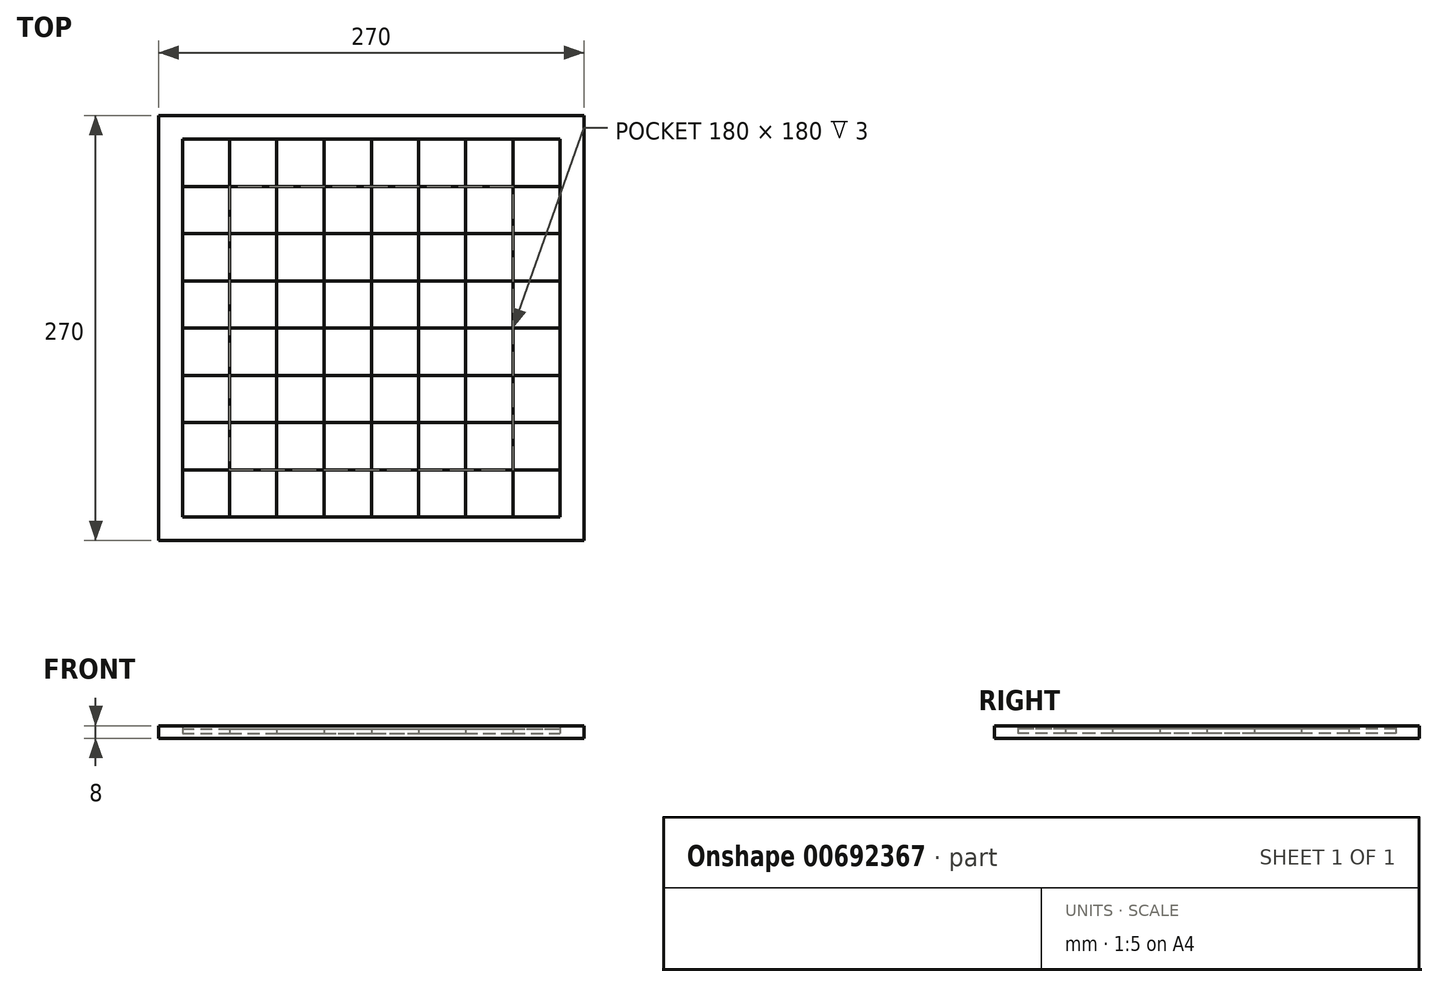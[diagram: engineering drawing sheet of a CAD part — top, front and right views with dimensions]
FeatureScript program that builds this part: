
annotation { "Feature Type Name" : "Feature", "Feature Type Description" : "" }
export const myFeature = defineFeature(function(context is Context, id is Id, definition is map)
    precondition{}
    {
        {
            var Q0;
            Q0=qCreatedBy(makeId("Top.planeOp"),FACE);
            var sketch = newSketch(context, id + "F0", { "sketchPlane" : qUnion([Q0])});
            skLineSegment(sketch, "E0.bottom", {"start": v(-120, 120) * mm, "end": v(120, 120) * mm});
            skLineSegment(sketch, "E0.top", {"start": v(-120, -120) * mm, "end": v(120, -120) * mm});
            skLineSegment(sketch, "E0.left", {"start": v(-120, 120) * mm, "end": v(-120, -120) * mm});
            skLineSegment(sketch, "E0.right", {"start": v(120, 120) * mm, "end": v(120, -120) * mm});
            skPoint(sketch, "E0.middle", {"position": v(0, 0) * mm});
            skLineSegment(sketch, "E1.0", {"start": v(-135, 135) * mm, "end": v(-135, -135) * mm});
            skLineSegment(sketch, "E1.1", {"start": v(-135, 135) * mm, "end": v(135, 135) * mm});
            skLineSegment(sketch, "E1.2", {"start": v(135, 135) * mm, "end": v(135, -135) * mm});
            skLineSegment(sketch, "E1.3", {"start": v(-135, -135) * mm, "end": v(135, -135) * mm});
            skLineSegment(sketch, "E2.0.1.0", {"start": v(-120, 90) * mm, "end": v(120, 90) * mm});
            skLineSegment(sketch, "E2.0.2.0", {"start": v(-120, 60) * mm, "end": v(120, 60) * mm});
            skLineSegment(sketch, "E2.0.3.0", {"start": v(-120, 30) * mm, "end": v(120, 30) * mm});
            skLineSegment(sketch, "E2.0.4.0", {"start": v(-120, 0) * mm, "end": v(120, 0) * mm});
            skLineSegment(sketch, "E2.0.5.0", {"start": v(-120, -30) * mm, "end": v(120, -30) * mm});
            skLineSegment(sketch, "E2.0.6.0", {"start": v(-120, -60) * mm, "end": v(120, -60) * mm});
            skLineSegment(sketch, "E2.0.7.0", {"start": v(-120, -90) * mm, "end": v(120, -90) * mm});
            skLineSegment(sketch, "E2.direction2", {"start": v(-120, 120) * mm, "end": v(-120, 90) * mm, "construction": true});
            skLineSegment(sketch, "E3.1.0.0", {"start": v(-90, 120) * mm, "end": v(-90, -120) * mm});
            skLineSegment(sketch, "E3.2.0.0", {"start": v(-60, 120) * mm, "end": v(-60, -120) * mm});
            skLineSegment(sketch, "E3.3.0.0", {"start": v(-30, 120) * mm, "end": v(-30, -120) * mm});
            skLineSegment(sketch, "E3.4.0.0", {"start": v(0, 120) * mm, "end": v(0, -120) * mm});
            skLineSegment(sketch, "E3.5.0.0", {"start": v(30, 120) * mm, "end": v(30, -120) * mm});
            skLineSegment(sketch, "E3.6.0.0", {"start": v(60, 120) * mm, "end": v(60, -120) * mm});
            skLineSegment(sketch, "E3.7.0.0", {"start": v(90, 120) * mm, "end": v(90, -120) * mm});
            skSolve(sketch);
        }
        {
            var Q0;
            {var subQ0=sQuery(id+"F0.wireOp",EDGE,"E3.2.0.0");var subQ1=sQuery(id+"F0.wireOp",EDGE,"E2.0.2.0");var subQ2=makeQuery(id+"F0.imprint","INTERSECT",VERTEX,{"derivedFrom":[subQ1,subQ0]});Q0=makeQuery(id+"F0.imprint","IMPRINT",FACE,{"disambiguationData":[TD([[makeQuery(id+"F0.imprint","IMPRINT",EDGE,{"disambiguationData":[TD([[subQ2,-1.0]])],"derivedFrom":subQ1}),-1.0]])]});}
            var Q1;
            {var subQ0=sQuery(id+"F0.wireOp",EDGE,"E0.right");var subQ1=sQuery(id+"F0.wireOp",EDGE,"E0.bottom");var subQ2=makeQuery(id+"F0.imprint","INTERSECT",VERTEX,{"derivedFrom":[subQ1,subQ0]});Q1=makeQuery(id+"F0.imprint","IMPRINT",FACE,{"disambiguationData":[TD([[makeQuery(id+"F0.imprint","IMPRINT",EDGE,{"disambiguationData":[TD([[subQ2,1.0]])],"derivedFrom":subQ1}),-1.0]])]});}
            var Q2;
            {var subQ0=sQuery(id+"F0.wireOp",EDGE,"E2.0.2.0");var subQ1=sQuery(id+"F0.wireOp",EDGE,"E0.right");var subQ2=makeQuery(id+"F0.imprint","INTERSECT",VERTEX,{"derivedFrom":[subQ1,subQ0]});Q2=makeQuery(id+"F0.imprint","IMPRINT",FACE,{"disambiguationData":[TD([[makeQuery(id+"F0.imprint","IMPRINT",EDGE,{"disambiguationData":[TD([[subQ2,-1.0]])],"derivedFrom":subQ1}),-1.0]])]});}
            var Q3;
            {var subQ0=sQuery(id+"F0.wireOp",EDGE,"E3.6.0.0");var subQ1=sQuery(id+"F0.wireOp",EDGE,"E2.0.4.0");var subQ2=makeQuery(id+"F0.imprint","INTERSECT",VERTEX,{"derivedFrom":[subQ1,subQ0]});Q3=makeQuery(id+"F0.imprint","IMPRINT",FACE,{"disambiguationData":[TD([[makeQuery(id+"F0.imprint","IMPRINT",EDGE,{"disambiguationData":[TD([[subQ2,-1.0]])],"derivedFrom":subQ1}),-1.0]])]});}
            var Q4;
            {var subQ0=sQuery(id+"F0.wireOp",EDGE,"E3.4.0.0");var subQ1=sQuery(id+"F0.wireOp",EDGE,"E0.top");var subQ2=makeQuery(id+"F0.imprint","INTERSECT",VERTEX,{"derivedFrom":[subQ1,subQ0]});Q4=makeQuery(id+"F0.imprint","IMPRINT",FACE,{"disambiguationData":[TD([[makeQuery(id+"F0.imprint","IMPRINT",EDGE,{"disambiguationData":[TD([[subQ2,-1.0]])],"derivedFrom":subQ1}),1.0]])]});}
            var Q5;
            {var subQ0=sQuery(id+"F0.wireOp",EDGE,"E3.5.0.0");var subQ1=sQuery(id+"F0.wireOp",EDGE,"E2.0.2.0");var subQ2=makeQuery(id+"F0.imprint","INTERSECT",VERTEX,{"derivedFrom":[subQ1,subQ0]});Q5=makeQuery(id+"F0.imprint","IMPRINT",FACE,{"disambiguationData":[TD([[makeQuery(id+"F0.imprint","IMPRINT",EDGE,{"disambiguationData":[TD([[subQ2,-1.0]])],"derivedFrom":subQ1}),-1.0]])]});}
            var Q6;
            {var subQ0=sQuery(id+"F0.wireOp",EDGE,"E2.0.1.0");var subQ1=sQuery(id+"F0.wireOp",EDGE,"E0.right");var subQ2=makeQuery(id+"F0.imprint","INTERSECT",VERTEX,{"derivedFrom":[subQ1,subQ0]});Q6=makeQuery(id+"F0.imprint","IMPRINT",FACE,{"disambiguationData":[TD([[makeQuery(id+"F0.imprint","IMPRINT",EDGE,{"disambiguationData":[TD([[subQ2,-1.0]])],"derivedFrom":subQ1}),-1.0]])]});}
            var Q7;
            {var subQ0=sQuery(id+"F0.wireOp",EDGE,"E3.3.0.0");var subQ1=sQuery(id+"F0.wireOp",EDGE,"E2.0.5.0");var subQ2=makeQuery(id+"F0.imprint","INTERSECT",VERTEX,{"derivedFrom":[subQ1,subQ0]});Q7=makeQuery(id+"F0.imprint","IMPRINT",FACE,{"disambiguationData":[TD([[makeQuery(id+"F0.imprint","IMPRINT",EDGE,{"disambiguationData":[TD([[subQ2,-1.0]])],"derivedFrom":subQ1}),-1.0]])]});}
            var Q8;
            {var subQ0=sQuery(id+"F0.wireOp",EDGE,"E0.right");var subQ1=sQuery(id+"F0.wireOp",EDGE,"E0.top");var subQ2=makeQuery(id+"F0.imprint","INTERSECT",VERTEX,{"derivedFrom":[subQ1,subQ0]});Q8=makeQuery(id+"F0.imprint","IMPRINT",FACE,{"disambiguationData":[TD([[makeQuery(id+"F0.imprint","IMPRINT",EDGE,{"disambiguationData":[TD([[subQ2,1.0]])],"derivedFrom":subQ1}),1.0]])]});}
            var Q9;
            {var subQ0=sQuery(id+"F0.wireOp",EDGE,"E0.left");var subQ1=sQuery(id+"F0.wireOp",EDGE,"E0.bottom");var subQ2=makeQuery(id+"F0.imprint","INTERSECT",VERTEX,{"derivedFrom":[subQ1,subQ0]});Q9=makeQuery(id+"F0.imprint","IMPRINT",FACE,{"disambiguationData":[TD([[makeQuery(id+"F0.imprint","IMPRINT",EDGE,{"disambiguationData":[TD([[subQ2,-1.0]])],"derivedFrom":subQ1}),-1.0]])]});}
            var Q10;
            {var subQ0=sQuery(id+"F0.wireOp",EDGE,"E3.3.0.0");var subQ1=sQuery(id+"F0.wireOp",EDGE,"E0.top");var subQ2=makeQuery(id+"F0.imprint","INTERSECT",VERTEX,{"derivedFrom":[subQ1,subQ0]});Q10=makeQuery(id+"F0.imprint","IMPRINT",FACE,{"disambiguationData":[TD([[makeQuery(id+"F0.imprint","IMPRINT",EDGE,{"disambiguationData":[TD([[subQ2,-1.0]])],"derivedFrom":subQ1}),1.0]])]});}
            var Q11;
            {var subQ0=sQuery(id+"F0.wireOp",EDGE,"E2.0.1.0");var subQ1=sQuery(id+"F0.wireOp",EDGE,"E0.left");var subQ2=makeQuery(id+"F0.imprint","INTERSECT",VERTEX,{"derivedFrom":[subQ1,subQ0]});Q11=makeQuery(id+"F0.imprint","IMPRINT",FACE,{"disambiguationData":[TD([[makeQuery(id+"F0.imprint","IMPRINT",EDGE,{"disambiguationData":[TD([[subQ2,-1.0]])],"derivedFrom":subQ1}),1.0]])]});}
            var Q12;
            {var subQ0=sQuery(id+"F0.wireOp",EDGE,"E2.0.5.0");var subQ1=sQuery(id+"F0.wireOp",EDGE,"E0.left");var subQ2=makeQuery(id+"F0.imprint","INTERSECT",VERTEX,{"derivedFrom":[subQ1,subQ0]});Q12=makeQuery(id+"F0.imprint","IMPRINT",FACE,{"disambiguationData":[TD([[makeQuery(id+"F0.imprint","IMPRINT",EDGE,{"disambiguationData":[TD([[subQ2,-1.0]])],"derivedFrom":subQ1}),1.0]])]});}
            var Q13;
            {var subQ0=sQuery(id+"F0.wireOp",EDGE,"E2.0.4.0");var subQ1=sQuery(id+"F0.wireOp",EDGE,"E0.left");var subQ2=makeQuery(id+"F0.imprint","INTERSECT",VERTEX,{"derivedFrom":[subQ1,subQ0]});Q13=makeQuery(id+"F0.imprint","IMPRINT",FACE,{"disambiguationData":[TD([[makeQuery(id+"F0.imprint","IMPRINT",EDGE,{"disambiguationData":[TD([[subQ2,-1.0]])],"derivedFrom":subQ1}),1.0]])]});}
            var Q14;
            {var subQ0=sQuery(id+"F0.wireOp",EDGE,"E3.5.0.0");var subQ1=sQuery(id+"F0.wireOp",EDGE,"E2.0.1.0");var subQ2=makeQuery(id+"F0.imprint","INTERSECT",VERTEX,{"derivedFrom":[subQ1,subQ0]});Q14=makeQuery(id+"F0.imprint","IMPRINT",FACE,{"disambiguationData":[TD([[makeQuery(id+"F0.imprint","IMPRINT",EDGE,{"disambiguationData":[TD([[subQ2,-1.0]])],"derivedFrom":subQ1}),-1.0]])]});}
            var Q15;
            {var subQ0=sQuery(id+"F0.wireOp",EDGE,"E2.0.5.0");var subQ1=sQuery(id+"F0.wireOp",EDGE,"E0.right");var subQ2=makeQuery(id+"F0.imprint","INTERSECT",VERTEX,{"derivedFrom":[subQ1,subQ0]});Q15=makeQuery(id+"F0.imprint","IMPRINT",FACE,{"disambiguationData":[TD([[makeQuery(id+"F0.imprint","IMPRINT",EDGE,{"disambiguationData":[TD([[subQ2,-1.0]])],"derivedFrom":subQ1}),-1.0]])]});}
            var Q16;
            {var subQ0=sQuery(id+"F0.wireOp",EDGE,"E3.3.0.0");var subQ1=sQuery(id+"F0.wireOp",EDGE,"E2.0.3.0");var subQ2=makeQuery(id+"F0.imprint","INTERSECT",VERTEX,{"derivedFrom":[subQ1,subQ0]});Q16=makeQuery(id+"F0.imprint","IMPRINT",FACE,{"disambiguationData":[TD([[makeQuery(id+"F0.imprint","IMPRINT",EDGE,{"disambiguationData":[TD([[subQ2,-1.0]])],"derivedFrom":subQ1}),-1.0]])]});}
            var Q17;
            {var subQ0=sQuery(id+"F0.wireOp",EDGE,"E0.left");var subQ1=sQuery(id+"F0.wireOp",EDGE,"E0.top");var subQ2=makeQuery(id+"F0.imprint","INTERSECT",VERTEX,{"derivedFrom":[subQ1,subQ0]});Q17=makeQuery(id+"F0.imprint","IMPRINT",FACE,{"disambiguationData":[TD([[makeQuery(id+"F0.imprint","IMPRINT",EDGE,{"disambiguationData":[TD([[subQ2,-1.0]])],"derivedFrom":subQ1}),1.0]])]});}
            var Q18;
            {var subQ0=sQuery(id+"F0.wireOp",EDGE,"E3.6.0.0");var subQ1=sQuery(id+"F0.wireOp",EDGE,"E0.bottom");var subQ2=makeQuery(id+"F0.imprint","INTERSECT",VERTEX,{"derivedFrom":[subQ1,subQ0]});Q18=makeQuery(id+"F0.imprint","IMPRINT",FACE,{"disambiguationData":[TD([[makeQuery(id+"F0.imprint","IMPRINT",EDGE,{"disambiguationData":[TD([[subQ2,-1.0]])],"derivedFrom":subQ1}),-1.0]])]});}
            var Q19;
            {var subQ0=sQuery(id+"F0.wireOp",EDGE,"E3.6.0.0");var subQ1=sQuery(id+"F0.wireOp",EDGE,"E2.0.2.0");var subQ2=makeQuery(id+"F0.imprint","INTERSECT",VERTEX,{"derivedFrom":[subQ1,subQ0]});Q19=makeQuery(id+"F0.imprint","IMPRINT",FACE,{"disambiguationData":[TD([[makeQuery(id+"F0.imprint","IMPRINT",EDGE,{"disambiguationData":[TD([[subQ2,-1.0]])],"derivedFrom":subQ1}),-1.0]])]});}
            var Q20;
            {var subQ0=sQuery(id+"F0.wireOp",EDGE,"E3.1.0.0");var subQ1=sQuery(id+"F0.wireOp",EDGE,"E2.0.6.0");var subQ2=makeQuery(id+"F0.imprint","INTERSECT",VERTEX,{"derivedFrom":[subQ1,subQ0]});Q20=makeQuery(id+"F0.imprint","IMPRINT",FACE,{"disambiguationData":[TD([[makeQuery(id+"F0.imprint","IMPRINT",EDGE,{"disambiguationData":[TD([[subQ2,-1.0]])],"derivedFrom":subQ1}),-1.0]])]});}
            var Q21;
            {var subQ0=sQuery(id+"F0.wireOp",EDGE,"E3.4.0.0");var subQ1=sQuery(id+"F0.wireOp",EDGE,"E2.0.3.0");var subQ2=makeQuery(id+"F0.imprint","INTERSECT",VERTEX,{"derivedFrom":[subQ1,subQ0]});Q21=makeQuery(id+"F0.imprint","IMPRINT",FACE,{"disambiguationData":[TD([[makeQuery(id+"F0.imprint","IMPRINT",EDGE,{"disambiguationData":[TD([[subQ2,-1.0]])],"derivedFrom":subQ1}),-1.0]])]});}
            var Q22;
            {var subQ0=sQuery(id+"F0.wireOp",EDGE,"E2.0.6.0");var subQ1=sQuery(id+"F0.wireOp",EDGE,"E0.left");var subQ2=makeQuery(id+"F0.imprint","INTERSECT",VERTEX,{"derivedFrom":[subQ1,subQ0]});Q22=makeQuery(id+"F0.imprint","IMPRINT",FACE,{"disambiguationData":[TD([[makeQuery(id+"F0.imprint","IMPRINT",EDGE,{"disambiguationData":[TD([[subQ2,-1.0]])],"derivedFrom":subQ1}),1.0]])]});}
            var Q23;
            {var subQ0=sQuery(id+"F0.wireOp",EDGE,"E3.1.0.0");var subQ1=sQuery(id+"F0.wireOp",EDGE,"E0.top");var subQ2=makeQuery(id+"F0.imprint","INTERSECT",VERTEX,{"derivedFrom":[subQ1,subQ0]});Q23=makeQuery(id+"F0.imprint","IMPRINT",FACE,{"disambiguationData":[TD([[makeQuery(id+"F0.imprint","IMPRINT",EDGE,{"disambiguationData":[TD([[subQ2,-1.0]])],"derivedFrom":subQ1}),1.0]])]});}
            var Q24;
            {var subQ0=sQuery(id+"F0.wireOp",EDGE,"E2.0.6.0");var subQ1=sQuery(id+"F0.wireOp",EDGE,"E0.right");var subQ2=makeQuery(id+"F0.imprint","INTERSECT",VERTEX,{"derivedFrom":[subQ1,subQ0]});Q24=makeQuery(id+"F0.imprint","IMPRINT",FACE,{"disambiguationData":[TD([[makeQuery(id+"F0.imprint","IMPRINT",EDGE,{"disambiguationData":[TD([[subQ2,-1.0]])],"derivedFrom":subQ1}),-1.0]])]});}
            var Q25;
            {var subQ0=sQuery(id+"F0.wireOp",EDGE,"E3.3.0.0");var subQ1=sQuery(id+"F0.wireOp",EDGE,"E2.0.4.0");var subQ2=makeQuery(id+"F0.imprint","INTERSECT",VERTEX,{"derivedFrom":[subQ1,subQ0]});Q25=makeQuery(id+"F0.imprint","IMPRINT",FACE,{"disambiguationData":[TD([[makeQuery(id+"F0.imprint","IMPRINT",EDGE,{"disambiguationData":[TD([[subQ2,-1.0]])],"derivedFrom":subQ1}),-1.0]])]});}
            var Q26;
            {var subQ0=sQuery(id+"F0.wireOp",EDGE,"E3.5.0.0");var subQ1=sQuery(id+"F0.wireOp",EDGE,"E0.top");var subQ2=makeQuery(id+"F0.imprint","INTERSECT",VERTEX,{"derivedFrom":[subQ1,subQ0]});Q26=makeQuery(id+"F0.imprint","IMPRINT",FACE,{"disambiguationData":[TD([[makeQuery(id+"F0.imprint","IMPRINT",EDGE,{"disambiguationData":[TD([[subQ2,-1.0]])],"derivedFrom":subQ1}),1.0]])]});}
            var Q27;
            {var subQ0=sQuery(id+"F0.wireOp",EDGE,"E3.2.0.0");var subQ1=sQuery(id+"F0.wireOp",EDGE,"E0.top");var subQ2=makeQuery(id+"F0.imprint","INTERSECT",VERTEX,{"derivedFrom":[subQ1,subQ0]});Q27=makeQuery(id+"F0.imprint","IMPRINT",FACE,{"disambiguationData":[TD([[makeQuery(id+"F0.imprint","IMPRINT",EDGE,{"disambiguationData":[TD([[subQ2,-1.0]])],"derivedFrom":subQ1}),1.0]])]});}
            var Q28;
            {var subQ0=sQuery(id+"F0.wireOp",EDGE,"E3.4.0.0");var subQ1=sQuery(id+"F0.wireOp",EDGE,"E2.0.6.0");var subQ2=makeQuery(id+"F0.imprint","INTERSECT",VERTEX,{"derivedFrom":[subQ1,subQ0]});Q28=makeQuery(id+"F0.imprint","IMPRINT",FACE,{"disambiguationData":[TD([[makeQuery(id+"F0.imprint","IMPRINT",EDGE,{"disambiguationData":[TD([[subQ2,-1.0]])],"derivedFrom":subQ1}),-1.0]])]});}
            var Q29;
            {var subQ0=sQuery(id+"F0.wireOp",EDGE,"E3.1.0.0");var subQ1=sQuery(id+"F0.wireOp",EDGE,"E2.0.5.0");var subQ2=makeQuery(id+"F0.imprint","INTERSECT",VERTEX,{"derivedFrom":[subQ1,subQ0]});Q29=makeQuery(id+"F0.imprint","IMPRINT",FACE,{"disambiguationData":[TD([[makeQuery(id+"F0.imprint","IMPRINT",EDGE,{"disambiguationData":[TD([[subQ2,-1.0]])],"derivedFrom":subQ1}),-1.0]])]});}
            var Q30;
            {var subQ0=sQuery(id+"F0.wireOp",EDGE,"E3.6.0.0");var subQ1=sQuery(id+"F0.wireOp",EDGE,"E2.0.3.0");var subQ2=makeQuery(id+"F0.imprint","INTERSECT",VERTEX,{"derivedFrom":[subQ1,subQ0]});Q30=makeQuery(id+"F0.imprint","IMPRINT",FACE,{"disambiguationData":[TD([[makeQuery(id+"F0.imprint","IMPRINT",EDGE,{"disambiguationData":[TD([[subQ2,-1.0]])],"derivedFrom":subQ1}),-1.0]])]});}
            var Q31;
            {var subQ0=sQuery(id+"F0.wireOp",EDGE,"E3.2.0.0");var subQ1=sQuery(id+"F0.wireOp",EDGE,"E2.0.1.0");var subQ2=makeQuery(id+"F0.imprint","INTERSECT",VERTEX,{"derivedFrom":[subQ1,subQ0]});Q31=makeQuery(id+"F0.imprint","IMPRINT",FACE,{"disambiguationData":[TD([[makeQuery(id+"F0.imprint","IMPRINT",EDGE,{"disambiguationData":[TD([[subQ2,-1.0]])],"derivedFrom":subQ1}),-1.0]])]});}
            var Q32;
            {var subQ0=sQuery(id+"F0.wireOp",EDGE,"E3.3.0.0");var subQ1=sQuery(id+"F0.wireOp",EDGE,"E2.0.2.0");var subQ2=makeQuery(id+"F0.imprint","INTERSECT",VERTEX,{"derivedFrom":[subQ1,subQ0]});Q32=makeQuery(id+"F0.imprint","IMPRINT",FACE,{"disambiguationData":[TD([[makeQuery(id+"F0.imprint","IMPRINT",EDGE,{"disambiguationData":[TD([[subQ2,-1.0]])],"derivedFrom":subQ1}),-1.0]])]});}
            var Q33;
            {var subQ0=sQuery(id+"F0.wireOp",EDGE,"E3.4.0.0");var subQ1=sQuery(id+"F0.wireOp",EDGE,"E2.0.5.0");var subQ2=makeQuery(id+"F0.imprint","INTERSECT",VERTEX,{"derivedFrom":[subQ1,subQ0]});Q33=makeQuery(id+"F0.imprint","IMPRINT",FACE,{"disambiguationData":[TD([[makeQuery(id+"F0.imprint","IMPRINT",EDGE,{"disambiguationData":[TD([[subQ2,-1.0]])],"derivedFrom":subQ1}),-1.0]])]});}
            var Q34;
            {var subQ0=sQuery(id+"F0.wireOp",EDGE,"E3.4.0.0");var subQ1=sQuery(id+"F0.wireOp",EDGE,"E0.bottom");var subQ2=makeQuery(id+"F0.imprint","INTERSECT",VERTEX,{"derivedFrom":[subQ1,subQ0]});Q34=makeQuery(id+"F0.imprint","IMPRINT",FACE,{"disambiguationData":[TD([[makeQuery(id+"F0.imprint","IMPRINT",EDGE,{"disambiguationData":[TD([[subQ2,-1.0]])],"derivedFrom":subQ1}),-1.0]])]});}
            var Q35;
            {var subQ0=sQuery(id+"F0.wireOp",EDGE,"E3.5.0.0");var subQ1=sQuery(id+"F0.wireOp",EDGE,"E0.bottom");var subQ2=makeQuery(id+"F0.imprint","INTERSECT",VERTEX,{"derivedFrom":[subQ1,subQ0]});Q35=makeQuery(id+"F0.imprint","IMPRINT",FACE,{"disambiguationData":[TD([[makeQuery(id+"F0.imprint","IMPRINT",EDGE,{"disambiguationData":[TD([[subQ2,-1.0]])],"derivedFrom":subQ1}),-1.0]])]});}
            var Q36;
            {var subQ0=sQuery(id+"F0.wireOp",EDGE,"E3.3.0.0");var subQ1=sQuery(id+"F0.wireOp",EDGE,"E0.bottom");var subQ2=makeQuery(id+"F0.imprint","INTERSECT",VERTEX,{"derivedFrom":[subQ1,subQ0]});Q36=makeQuery(id+"F0.imprint","IMPRINT",FACE,{"disambiguationData":[TD([[makeQuery(id+"F0.imprint","IMPRINT",EDGE,{"disambiguationData":[TD([[subQ2,-1.0]])],"derivedFrom":subQ1}),-1.0]])]});}
            var Q37;
            {var subQ0=sQuery(id+"F0.wireOp",EDGE,"E3.2.0.0");var subQ1=sQuery(id+"F0.wireOp",EDGE,"E0.bottom");var subQ2=makeQuery(id+"F0.imprint","INTERSECT",VERTEX,{"derivedFrom":[subQ1,subQ0]});Q37=makeQuery(id+"F0.imprint","IMPRINT",FACE,{"disambiguationData":[TD([[makeQuery(id+"F0.imprint","IMPRINT",EDGE,{"disambiguationData":[TD([[subQ2,-1.0]])],"derivedFrom":subQ1}),-1.0]])]});}
            var Q38;
            {var subQ0=sQuery(id+"F0.wireOp",EDGE,"E3.6.0.0");var subQ1=sQuery(id+"F0.wireOp",EDGE,"E0.top");var subQ2=makeQuery(id+"F0.imprint","INTERSECT",VERTEX,{"derivedFrom":[subQ1,subQ0]});Q38=makeQuery(id+"F0.imprint","IMPRINT",FACE,{"disambiguationData":[TD([[makeQuery(id+"F0.imprint","IMPRINT",EDGE,{"disambiguationData":[TD([[subQ2,-1.0]])],"derivedFrom":subQ1}),1.0]])]});}
            var Q39;
            {var subQ0=sQuery(id+"F0.wireOp",EDGE,"E3.2.0.0");var subQ1=sQuery(id+"F0.wireOp",EDGE,"E2.0.6.0");var subQ2=makeQuery(id+"F0.imprint","INTERSECT",VERTEX,{"derivedFrom":[subQ1,subQ0]});Q39=makeQuery(id+"F0.imprint","IMPRINT",FACE,{"disambiguationData":[TD([[makeQuery(id+"F0.imprint","IMPRINT",EDGE,{"disambiguationData":[TD([[subQ2,-1.0]])],"derivedFrom":subQ1}),-1.0]])]});}
            var Q40;
            {var subQ0=sQuery(id+"F0.wireOp",EDGE,"E3.1.0.0");var subQ1=sQuery(id+"F0.wireOp",EDGE,"E0.bottom");var subQ2=makeQuery(id+"F0.imprint","INTERSECT",VERTEX,{"derivedFrom":[subQ1,subQ0]});Q40=makeQuery(id+"F0.imprint","IMPRINT",FACE,{"disambiguationData":[TD([[makeQuery(id+"F0.imprint","IMPRINT",EDGE,{"disambiguationData":[TD([[subQ2,-1.0]])],"derivedFrom":subQ1}),-1.0]])]});}
            var Q41;
            {var subQ0=sQuery(id+"F0.wireOp",EDGE,"E3.5.0.0");var subQ1=sQuery(id+"F0.wireOp",EDGE,"E2.0.6.0");var subQ2=makeQuery(id+"F0.imprint","INTERSECT",VERTEX,{"derivedFrom":[subQ1,subQ0]});Q41=makeQuery(id+"F0.imprint","IMPRINT",FACE,{"disambiguationData":[TD([[makeQuery(id+"F0.imprint","IMPRINT",EDGE,{"disambiguationData":[TD([[subQ2,-1.0]])],"derivedFrom":subQ1}),-1.0]])]});}
            var Q42;
            {var subQ0=sQuery(id+"F0.wireOp",EDGE,"E3.2.0.0");var subQ1=sQuery(id+"F0.wireOp",EDGE,"E2.0.5.0");var subQ2=makeQuery(id+"F0.imprint","INTERSECT",VERTEX,{"derivedFrom":[subQ1,subQ0]});Q42=makeQuery(id+"F0.imprint","IMPRINT",FACE,{"disambiguationData":[TD([[makeQuery(id+"F0.imprint","IMPRINT",EDGE,{"disambiguationData":[TD([[subQ2,-1.0]])],"derivedFrom":subQ1}),-1.0]])]});}
            var Q43;
            {var subQ0=sQuery(id+"F0.wireOp",EDGE,"E3.1.0.0");var subQ1=sQuery(id+"F0.wireOp",EDGE,"E2.0.4.0");var subQ2=makeQuery(id+"F0.imprint","INTERSECT",VERTEX,{"derivedFrom":[subQ1,subQ0]});Q43=makeQuery(id+"F0.imprint","IMPRINT",FACE,{"disambiguationData":[TD([[makeQuery(id+"F0.imprint","IMPRINT",EDGE,{"disambiguationData":[TD([[subQ2,-1.0]])],"derivedFrom":subQ1}),-1.0]])]});}
            var Q44;
            {var subQ0=sQuery(id+"F0.wireOp",EDGE,"E3.3.0.0");var subQ1=sQuery(id+"F0.wireOp",EDGE,"E2.0.1.0");var subQ2=makeQuery(id+"F0.imprint","INTERSECT",VERTEX,{"derivedFrom":[subQ1,subQ0]});Q44=makeQuery(id+"F0.imprint","IMPRINT",FACE,{"disambiguationData":[TD([[makeQuery(id+"F0.imprint","IMPRINT",EDGE,{"disambiguationData":[TD([[subQ2,-1.0]])],"derivedFrom":subQ1}),-1.0]])]});}
            var Q45;
            {var subQ0=sQuery(id+"F0.wireOp",EDGE,"E3.4.0.0");var subQ1=sQuery(id+"F0.wireOp",EDGE,"E2.0.2.0");var subQ2=makeQuery(id+"F0.imprint","INTERSECT",VERTEX,{"derivedFrom":[subQ1,subQ0]});Q45=makeQuery(id+"F0.imprint","IMPRINT",FACE,{"disambiguationData":[TD([[makeQuery(id+"F0.imprint","IMPRINT",EDGE,{"disambiguationData":[TD([[subQ2,-1.0]])],"derivedFrom":subQ1}),-1.0]])]});}
            var Q46;
            {var subQ0=sQuery(id+"F0.wireOp",EDGE,"E2.0.2.0");var subQ1=sQuery(id+"F0.wireOp",EDGE,"E0.left");var subQ2=makeQuery(id+"F0.imprint","INTERSECT",VERTEX,{"derivedFrom":[subQ1,subQ0]});Q46=makeQuery(id+"F0.imprint","IMPRINT",FACE,{"disambiguationData":[TD([[makeQuery(id+"F0.imprint","IMPRINT",EDGE,{"disambiguationData":[TD([[subQ2,-1.0]])],"derivedFrom":subQ1}),1.0]])]});}
            var Q47;
            {var subQ0=sQuery(id+"F0.wireOp",EDGE,"E3.4.0.0");var subQ1=sQuery(id+"F0.wireOp",EDGE,"E2.0.4.0");var subQ2=makeQuery(id+"F0.imprint","INTERSECT",VERTEX,{"derivedFrom":[subQ1,subQ0]});Q47=makeQuery(id+"F0.imprint","IMPRINT",FACE,{"disambiguationData":[TD([[makeQuery(id+"F0.imprint","IMPRINT",EDGE,{"disambiguationData":[TD([[subQ2,-1.0]])],"derivedFrom":subQ1}),-1.0]])]});}
            var Q48;
            {var subQ0=sQuery(id+"F0.wireOp",EDGE,"E3.6.0.0");var subQ1=sQuery(id+"F0.wireOp",EDGE,"E2.0.1.0");var subQ2=makeQuery(id+"F0.imprint","INTERSECT",VERTEX,{"derivedFrom":[subQ1,subQ0]});Q48=makeQuery(id+"F0.imprint","IMPRINT",FACE,{"disambiguationData":[TD([[makeQuery(id+"F0.imprint","IMPRINT",EDGE,{"disambiguationData":[TD([[subQ2,-1.0]])],"derivedFrom":subQ1}),-1.0]])]});}
            var Q49;
            {var subQ0=sQuery(id+"F0.wireOp",EDGE,"E3.3.0.0");var subQ1=sQuery(id+"F0.wireOp",EDGE,"E2.0.6.0");var subQ2=makeQuery(id+"F0.imprint","INTERSECT",VERTEX,{"derivedFrom":[subQ1,subQ0]});Q49=makeQuery(id+"F0.imprint","IMPRINT",FACE,{"disambiguationData":[TD([[makeQuery(id+"F0.imprint","IMPRINT",EDGE,{"disambiguationData":[TD([[subQ2,-1.0]])],"derivedFrom":subQ1}),-1.0]])]});}
            var Q50;
            {var subQ0=sQuery(id+"F0.wireOp",EDGE,"E3.5.0.0");var subQ1=sQuery(id+"F0.wireOp",EDGE,"E2.0.3.0");var subQ2=makeQuery(id+"F0.imprint","INTERSECT",VERTEX,{"derivedFrom":[subQ1,subQ0]});Q50=makeQuery(id+"F0.imprint","IMPRINT",FACE,{"disambiguationData":[TD([[makeQuery(id+"F0.imprint","IMPRINT",EDGE,{"disambiguationData":[TD([[subQ2,-1.0]])],"derivedFrom":subQ1}),-1.0]])]});}
            var Q51;
            {var subQ0=sQuery(id+"F0.wireOp",EDGE,"E3.1.0.0");var subQ1=sQuery(id+"F0.wireOp",EDGE,"E2.0.1.0");var subQ2=makeQuery(id+"F0.imprint","INTERSECT",VERTEX,{"derivedFrom":[subQ1,subQ0]});Q51=makeQuery(id+"F0.imprint","IMPRINT",FACE,{"disambiguationData":[TD([[makeQuery(id+"F0.imprint","IMPRINT",EDGE,{"disambiguationData":[TD([[subQ2,-1.0]])],"derivedFrom":subQ1}),-1.0]])]});}
            var Q52;
            {var subQ0=sQuery(id+"F0.wireOp",EDGE,"E3.5.0.0");var subQ1=sQuery(id+"F0.wireOp",EDGE,"E2.0.5.0");var subQ2=makeQuery(id+"F0.imprint","INTERSECT",VERTEX,{"derivedFrom":[subQ1,subQ0]});Q52=makeQuery(id+"F0.imprint","IMPRINT",FACE,{"disambiguationData":[TD([[makeQuery(id+"F0.imprint","IMPRINT",EDGE,{"disambiguationData":[TD([[subQ2,-1.0]])],"derivedFrom":subQ1}),-1.0]])]});}
            var Q53;
            {var subQ0=sQuery(id+"F0.wireOp",EDGE,"E3.1.0.0");var subQ1=sQuery(id+"F0.wireOp",EDGE,"E2.0.3.0");var subQ2=makeQuery(id+"F0.imprint","INTERSECT",VERTEX,{"derivedFrom":[subQ1,subQ0]});Q53=makeQuery(id+"F0.imprint","IMPRINT",FACE,{"disambiguationData":[TD([[makeQuery(id+"F0.imprint","IMPRINT",EDGE,{"disambiguationData":[TD([[subQ2,-1.0]])],"derivedFrom":subQ1}),-1.0]])]});}
            var Q54;
            {var subQ0=sQuery(id+"F0.wireOp",EDGE,"E2.0.3.0");var subQ1=sQuery(id+"F0.wireOp",EDGE,"E0.right");var subQ2=makeQuery(id+"F0.imprint","INTERSECT",VERTEX,{"derivedFrom":[subQ1,subQ0]});Q54=makeQuery(id+"F0.imprint","IMPRINT",FACE,{"disambiguationData":[TD([[makeQuery(id+"F0.imprint","IMPRINT",EDGE,{"disambiguationData":[TD([[subQ2,-1.0]])],"derivedFrom":subQ1}),-1.0]])]});}
            var Q55;
            {var subQ0=sQuery(id+"F0.wireOp",EDGE,"E2.0.3.0");var subQ1=sQuery(id+"F0.wireOp",EDGE,"E0.left");var subQ2=makeQuery(id+"F0.imprint","INTERSECT",VERTEX,{"derivedFrom":[subQ1,subQ0]});Q55=makeQuery(id+"F0.imprint","IMPRINT",FACE,{"disambiguationData":[TD([[makeQuery(id+"F0.imprint","IMPRINT",EDGE,{"disambiguationData":[TD([[subQ2,-1.0]])],"derivedFrom":subQ1}),1.0]])]});}
            var Q56;
            {var subQ0=sQuery(id+"F0.wireOp",EDGE,"E3.5.0.0");var subQ1=sQuery(id+"F0.wireOp",EDGE,"E2.0.4.0");var subQ2=makeQuery(id+"F0.imprint","INTERSECT",VERTEX,{"derivedFrom":[subQ1,subQ0]});Q56=makeQuery(id+"F0.imprint","IMPRINT",FACE,{"disambiguationData":[TD([[makeQuery(id+"F0.imprint","IMPRINT",EDGE,{"disambiguationData":[TD([[subQ2,-1.0]])],"derivedFrom":subQ1}),-1.0]])]});}
            var Q57;
            {var subQ0=sQuery(id+"F0.wireOp",EDGE,"E3.1.0.0");var subQ1=sQuery(id+"F0.wireOp",EDGE,"E2.0.2.0");var subQ2=makeQuery(id+"F0.imprint","INTERSECT",VERTEX,{"derivedFrom":[subQ1,subQ0]});Q57=makeQuery(id+"F0.imprint","IMPRINT",FACE,{"disambiguationData":[TD([[makeQuery(id+"F0.imprint","IMPRINT",EDGE,{"disambiguationData":[TD([[subQ2,-1.0]])],"derivedFrom":subQ1}),-1.0]])]});}
            var Q58;
            {var subQ0=sQuery(id+"F0.wireOp",EDGE,"E3.6.0.0");var subQ1=sQuery(id+"F0.wireOp",EDGE,"E2.0.5.0");var subQ2=makeQuery(id+"F0.imprint","INTERSECT",VERTEX,{"derivedFrom":[subQ1,subQ0]});Q58=makeQuery(id+"F0.imprint","IMPRINT",FACE,{"disambiguationData":[TD([[makeQuery(id+"F0.imprint","IMPRINT",EDGE,{"disambiguationData":[TD([[subQ2,-1.0]])],"derivedFrom":subQ1}),-1.0]])]});}
            var Q59;
            {var subQ0=sQuery(id+"F0.wireOp",EDGE,"E3.4.0.0");var subQ1=sQuery(id+"F0.wireOp",EDGE,"E2.0.1.0");var subQ2=makeQuery(id+"F0.imprint","INTERSECT",VERTEX,{"derivedFrom":[subQ1,subQ0]});Q59=makeQuery(id+"F0.imprint","IMPRINT",FACE,{"disambiguationData":[TD([[makeQuery(id+"F0.imprint","IMPRINT",EDGE,{"disambiguationData":[TD([[subQ2,-1.0]])],"derivedFrom":subQ1}),-1.0]])]});}
            var Q60;
            {var subQ0=sQuery(id+"F0.wireOp",EDGE,"E3.2.0.0");var subQ1=sQuery(id+"F0.wireOp",EDGE,"E2.0.3.0");var subQ2=makeQuery(id+"F0.imprint","INTERSECT",VERTEX,{"derivedFrom":[subQ1,subQ0]});Q60=makeQuery(id+"F0.imprint","IMPRINT",FACE,{"disambiguationData":[TD([[makeQuery(id+"F0.imprint","IMPRINT",EDGE,{"disambiguationData":[TD([[subQ2,-1.0]])],"derivedFrom":subQ1}),-1.0]])]});}
            var Q61;
            {var subQ0=sQuery(id+"F0.wireOp",EDGE,"E2.0.4.0");var subQ1=sQuery(id+"F0.wireOp",EDGE,"E0.right");var subQ2=makeQuery(id+"F0.imprint","INTERSECT",VERTEX,{"derivedFrom":[subQ1,subQ0]});Q61=makeQuery(id+"F0.imprint","IMPRINT",FACE,{"disambiguationData":[TD([[makeQuery(id+"F0.imprint","IMPRINT",EDGE,{"disambiguationData":[TD([[subQ2,-1.0]])],"derivedFrom":subQ1}),-1.0]])]});}
            var Q62;
            {var subQ0=sQuery(id+"F0.wireOp",EDGE,"E3.6.0.0");var subQ1=sQuery(id+"F0.wireOp",EDGE,"E2.0.6.0");var subQ2=makeQuery(id+"F0.imprint","INTERSECT",VERTEX,{"derivedFrom":[subQ1,subQ0]});Q62=makeQuery(id+"F0.imprint","IMPRINT",FACE,{"disambiguationData":[TD([[makeQuery(id+"F0.imprint","IMPRINT",EDGE,{"disambiguationData":[TD([[subQ2,-1.0]])],"derivedFrom":subQ1}),-1.0]])]});}
            var Q63;
            {var subQ0=sQuery(id+"F0.wireOp",EDGE,"E3.2.0.0");var subQ1=sQuery(id+"F0.wireOp",EDGE,"E2.0.4.0");var subQ2=makeQuery(id+"F0.imprint","INTERSECT",VERTEX,{"derivedFrom":[subQ1,subQ0]});Q63=makeQuery(id+"F0.imprint","IMPRINT",FACE,{"disambiguationData":[TD([[makeQuery(id+"F0.imprint","IMPRINT",EDGE,{"disambiguationData":[TD([[subQ2,-1.0]])],"derivedFrom":subQ1}),-1.0]])]});}
            extrude(context, id + "F1", {"entities" : qUnion([Q0, Q1, Q2, Q3, Q4, Q5, Q6, Q7, Q8, Q9, Q10, Q11, Q12, Q13, Q14, Q15, Q16, Q17, Q18, Q19, Q20, Q21, Q22, Q23, Q24, Q25, Q26, Q27, Q28, Q29, Q30, Q31, Q32, Q33, Q34, Q35, Q36, Q37, Q38, Q39, Q40, Q41, Q42, Q43, Q44, Q45, Q46, Q47, Q48, Q49, Q50, Q51, Q52, Q53, Q54, Q55, Q56, Q57, Q58, Q59, Q60, Q61, Q62, Q63]), "depth" : 3 * mm, "offsetDistance" : 25 * mm});
        }
        {
            var Q0;
            Q0=makeQuery(id+"F0.imprint","IMPRINT",FACE,{"disambiguationData":[TD([[makeQuery(id+"F0.imprint","IMPRINT",EDGE,{"derivedFrom":sQuery(id+"F0.wireOp",EDGE,"E1.0")}),1.0]])]});
            extrude(context, id + "F2", {"entities" : qUnion([Q0]), "operationType" : NewBodyOperationType.ADD, "depth" : 8 * mm, "offsetDistance" : 25 * mm});
        }
        {
            var Q0;
            {var subQ0=sQuery(id+"F0.wireOp",EDGE,"E0.left");var subQ1=sQuery(id+"F0.wireOp",EDGE,"E0.bottom");var subQ2=makeQuery(id+"F0.imprint","INTERSECT",VERTEX,{"derivedFrom":[subQ1,subQ0]});Q0=makeQuery(id+"F0.imprint","IMPRINT",FACE,{"disambiguationData":[TD([[makeQuery(id+"F0.imprint","IMPRINT",EDGE,{"disambiguationData":[TD([[subQ2,-1.0]])],"derivedFrom":subQ1}),-1.0]])]});}
            var Q1;
            {var subQ0=sQuery(id+"F0.wireOp",EDGE,"E3.1.0.0");var subQ1=sQuery(id+"F0.wireOp",EDGE,"E2.0.1.0");var subQ2=makeQuery(id+"F0.imprint","INTERSECT",VERTEX,{"derivedFrom":[subQ1,subQ0]});Q1=makeQuery(id+"F0.imprint","IMPRINT",FACE,{"disambiguationData":[TD([[makeQuery(id+"F0.imprint","IMPRINT",EDGE,{"disambiguationData":[TD([[subQ2,-1.0]])],"derivedFrom":subQ1}),-1.0]])]});}
            var Q2;
            {var subQ0=sQuery(id+"F0.wireOp",EDGE,"E3.2.0.0");var subQ1=sQuery(id+"F0.wireOp",EDGE,"E0.bottom");var subQ2=makeQuery(id+"F0.imprint","INTERSECT",VERTEX,{"derivedFrom":[subQ1,subQ0]});Q2=makeQuery(id+"F0.imprint","IMPRINT",FACE,{"disambiguationData":[TD([[makeQuery(id+"F0.imprint","IMPRINT",EDGE,{"disambiguationData":[TD([[subQ2,-1.0]])],"derivedFrom":subQ1}),-1.0]])]});}
            var Q3;
            {var subQ0=sQuery(id+"F0.wireOp",EDGE,"E3.3.0.0");var subQ1=sQuery(id+"F0.wireOp",EDGE,"E2.0.1.0");var subQ2=makeQuery(id+"F0.imprint","INTERSECT",VERTEX,{"derivedFrom":[subQ1,subQ0]});Q3=makeQuery(id+"F0.imprint","IMPRINT",FACE,{"disambiguationData":[TD([[makeQuery(id+"F0.imprint","IMPRINT",EDGE,{"disambiguationData":[TD([[subQ2,-1.0]])],"derivedFrom":subQ1}),-1.0]])]});}
            var Q4;
            {var subQ0=sQuery(id+"F0.wireOp",EDGE,"E3.4.0.0");var subQ1=sQuery(id+"F0.wireOp",EDGE,"E0.bottom");var subQ2=makeQuery(id+"F0.imprint","INTERSECT",VERTEX,{"derivedFrom":[subQ1,subQ0]});Q4=makeQuery(id+"F0.imprint","IMPRINT",FACE,{"disambiguationData":[TD([[makeQuery(id+"F0.imprint","IMPRINT",EDGE,{"disambiguationData":[TD([[subQ2,-1.0]])],"derivedFrom":subQ1}),-1.0]])]});}
            var Q5;
            {var subQ0=sQuery(id+"F0.wireOp",EDGE,"E3.5.0.0");var subQ1=sQuery(id+"F0.wireOp",EDGE,"E2.0.1.0");var subQ2=makeQuery(id+"F0.imprint","INTERSECT",VERTEX,{"derivedFrom":[subQ1,subQ0]});Q5=makeQuery(id+"F0.imprint","IMPRINT",FACE,{"disambiguationData":[TD([[makeQuery(id+"F0.imprint","IMPRINT",EDGE,{"disambiguationData":[TD([[subQ2,-1.0]])],"derivedFrom":subQ1}),-1.0]])]});}
            var Q6;
            {var subQ0=sQuery(id+"F0.wireOp",EDGE,"E3.6.0.0");var subQ1=sQuery(id+"F0.wireOp",EDGE,"E2.0.2.0");var subQ2=makeQuery(id+"F0.imprint","INTERSECT",VERTEX,{"derivedFrom":[subQ1,subQ0]});Q6=makeQuery(id+"F0.imprint","IMPRINT",FACE,{"disambiguationData":[TD([[makeQuery(id+"F0.imprint","IMPRINT",EDGE,{"disambiguationData":[TD([[subQ2,-1.0]])],"derivedFrom":subQ1}),-1.0]])]});}
            var Q7;
            {var subQ0=sQuery(id+"F0.wireOp",EDGE,"E2.0.3.0");var subQ1=sQuery(id+"F0.wireOp",EDGE,"E0.right");var subQ2=makeQuery(id+"F0.imprint","INTERSECT",VERTEX,{"derivedFrom":[subQ1,subQ0]});Q7=makeQuery(id+"F0.imprint","IMPRINT",FACE,{"disambiguationData":[TD([[makeQuery(id+"F0.imprint","IMPRINT",EDGE,{"disambiguationData":[TD([[subQ2,-1.0]])],"derivedFrom":subQ1}),-1.0]])]});}
            var Q8;
            {var subQ0=sQuery(id+"F0.wireOp",EDGE,"E2.0.1.0");var subQ1=sQuery(id+"F0.wireOp",EDGE,"E0.right");var subQ2=makeQuery(id+"F0.imprint","INTERSECT",VERTEX,{"derivedFrom":[subQ1,subQ0]});Q8=makeQuery(id+"F0.imprint","IMPRINT",FACE,{"disambiguationData":[TD([[makeQuery(id+"F0.imprint","IMPRINT",EDGE,{"disambiguationData":[TD([[subQ2,-1.0]])],"derivedFrom":subQ1}),-1.0]])]});}
            var Q9;
            {var subQ0=sQuery(id+"F0.wireOp",EDGE,"E3.6.0.0");var subQ1=sQuery(id+"F0.wireOp",EDGE,"E0.bottom");var subQ2=makeQuery(id+"F0.imprint","INTERSECT",VERTEX,{"derivedFrom":[subQ1,subQ0]});Q9=makeQuery(id+"F0.imprint","IMPRINT",FACE,{"disambiguationData":[TD([[makeQuery(id+"F0.imprint","IMPRINT",EDGE,{"disambiguationData":[TD([[subQ2,-1.0]])],"derivedFrom":subQ1}),-1.0]])]});}
            var Q10;
            {var subQ0=sQuery(id+"F0.wireOp",EDGE,"E3.6.0.0");var subQ1=sQuery(id+"F0.wireOp",EDGE,"E2.0.4.0");var subQ2=makeQuery(id+"F0.imprint","INTERSECT",VERTEX,{"derivedFrom":[subQ1,subQ0]});Q10=makeQuery(id+"F0.imprint","IMPRINT",FACE,{"disambiguationData":[TD([[makeQuery(id+"F0.imprint","IMPRINT",EDGE,{"disambiguationData":[TD([[subQ2,-1.0]])],"derivedFrom":subQ1}),-1.0]])]});}
            var Q11;
            {var subQ0=sQuery(id+"F0.wireOp",EDGE,"E3.5.0.0");var subQ1=sQuery(id+"F0.wireOp",EDGE,"E2.0.3.0");var subQ2=makeQuery(id+"F0.imprint","INTERSECT",VERTEX,{"derivedFrom":[subQ1,subQ0]});Q11=makeQuery(id+"F0.imprint","IMPRINT",FACE,{"disambiguationData":[TD([[makeQuery(id+"F0.imprint","IMPRINT",EDGE,{"disambiguationData":[TD([[subQ2,-1.0]])],"derivedFrom":subQ1}),-1.0]])]});}
            var Q12;
            {var subQ0=sQuery(id+"F0.wireOp",EDGE,"E3.4.0.0");var subQ1=sQuery(id+"F0.wireOp",EDGE,"E2.0.2.0");var subQ2=makeQuery(id+"F0.imprint","INTERSECT",VERTEX,{"derivedFrom":[subQ1,subQ0]});Q12=makeQuery(id+"F0.imprint","IMPRINT",FACE,{"disambiguationData":[TD([[makeQuery(id+"F0.imprint","IMPRINT",EDGE,{"disambiguationData":[TD([[subQ2,-1.0]])],"derivedFrom":subQ1}),-1.0]])]});}
            var Q13;
            {var subQ0=sQuery(id+"F0.wireOp",EDGE,"E3.2.0.0");var subQ1=sQuery(id+"F0.wireOp",EDGE,"E2.0.2.0");var subQ2=makeQuery(id+"F0.imprint","INTERSECT",VERTEX,{"derivedFrom":[subQ1,subQ0]});Q13=makeQuery(id+"F0.imprint","IMPRINT",FACE,{"disambiguationData":[TD([[makeQuery(id+"F0.imprint","IMPRINT",EDGE,{"disambiguationData":[TD([[subQ2,-1.0]])],"derivedFrom":subQ1}),-1.0]])]});}
            var Q14;
            {var subQ0=sQuery(id+"F0.wireOp",EDGE,"E2.0.2.0");var subQ1=sQuery(id+"F0.wireOp",EDGE,"E0.left");var subQ2=makeQuery(id+"F0.imprint","INTERSECT",VERTEX,{"derivedFrom":[subQ1,subQ0]});Q14=makeQuery(id+"F0.imprint","IMPRINT",FACE,{"disambiguationData":[TD([[makeQuery(id+"F0.imprint","IMPRINT",EDGE,{"disambiguationData":[TD([[subQ2,-1.0]])],"derivedFrom":subQ1}),1.0]])]});}
            var Q15;
            {var subQ0=sQuery(id+"F0.wireOp",EDGE,"E3.1.0.0");var subQ1=sQuery(id+"F0.wireOp",EDGE,"E2.0.3.0");var subQ2=makeQuery(id+"F0.imprint","INTERSECT",VERTEX,{"derivedFrom":[subQ1,subQ0]});Q15=makeQuery(id+"F0.imprint","IMPRINT",FACE,{"disambiguationData":[TD([[makeQuery(id+"F0.imprint","IMPRINT",EDGE,{"disambiguationData":[TD([[subQ2,-1.0]])],"derivedFrom":subQ1}),-1.0]])]});}
            var Q16;
            {var subQ0=sQuery(id+"F0.wireOp",EDGE,"E3.2.0.0");var subQ1=sQuery(id+"F0.wireOp",EDGE,"E2.0.4.0");var subQ2=makeQuery(id+"F0.imprint","INTERSECT",VERTEX,{"derivedFrom":[subQ1,subQ0]});Q16=makeQuery(id+"F0.imprint","IMPRINT",FACE,{"disambiguationData":[TD([[makeQuery(id+"F0.imprint","IMPRINT",EDGE,{"disambiguationData":[TD([[subQ2,-1.0]])],"derivedFrom":subQ1}),-1.0]])]});}
            var Q17;
            {var subQ0=sQuery(id+"F0.wireOp",EDGE,"E3.3.0.0");var subQ1=sQuery(id+"F0.wireOp",EDGE,"E2.0.3.0");var subQ2=makeQuery(id+"F0.imprint","INTERSECT",VERTEX,{"derivedFrom":[subQ1,subQ0]});Q17=makeQuery(id+"F0.imprint","IMPRINT",FACE,{"disambiguationData":[TD([[makeQuery(id+"F0.imprint","IMPRINT",EDGE,{"disambiguationData":[TD([[subQ2,-1.0]])],"derivedFrom":subQ1}),-1.0]])]});}
            var Q18;
            {var subQ0=sQuery(id+"F0.wireOp",EDGE,"E3.4.0.0");var subQ1=sQuery(id+"F0.wireOp",EDGE,"E2.0.4.0");var subQ2=makeQuery(id+"F0.imprint","INTERSECT",VERTEX,{"derivedFrom":[subQ1,subQ0]});Q18=makeQuery(id+"F0.imprint","IMPRINT",FACE,{"disambiguationData":[TD([[makeQuery(id+"F0.imprint","IMPRINT",EDGE,{"disambiguationData":[TD([[subQ2,-1.0]])],"derivedFrom":subQ1}),-1.0]])]});}
            var Q19;
            {var subQ0=sQuery(id+"F0.wireOp",EDGE,"E3.5.0.0");var subQ1=sQuery(id+"F0.wireOp",EDGE,"E2.0.5.0");var subQ2=makeQuery(id+"F0.imprint","INTERSECT",VERTEX,{"derivedFrom":[subQ1,subQ0]});Q19=makeQuery(id+"F0.imprint","IMPRINT",FACE,{"disambiguationData":[TD([[makeQuery(id+"F0.imprint","IMPRINT",EDGE,{"disambiguationData":[TD([[subQ2,-1.0]])],"derivedFrom":subQ1}),-1.0]])]});}
            var Q20;
            {var subQ0=sQuery(id+"F0.wireOp",EDGE,"E3.6.0.0");var subQ1=sQuery(id+"F0.wireOp",EDGE,"E2.0.6.0");var subQ2=makeQuery(id+"F0.imprint","INTERSECT",VERTEX,{"derivedFrom":[subQ1,subQ0]});Q20=makeQuery(id+"F0.imprint","IMPRINT",FACE,{"disambiguationData":[TD([[makeQuery(id+"F0.imprint","IMPRINT",EDGE,{"disambiguationData":[TD([[subQ2,-1.0]])],"derivedFrom":subQ1}),-1.0]])]});}
            var Q21;
            {var subQ0=sQuery(id+"F0.wireOp",EDGE,"E0.right");var subQ1=sQuery(id+"F0.wireOp",EDGE,"E0.top");var subQ2=makeQuery(id+"F0.imprint","INTERSECT",VERTEX,{"derivedFrom":[subQ1,subQ0]});Q21=makeQuery(id+"F0.imprint","IMPRINT",FACE,{"disambiguationData":[TD([[makeQuery(id+"F0.imprint","IMPRINT",EDGE,{"disambiguationData":[TD([[subQ2,1.0]])],"derivedFrom":subQ1}),1.0]])]});}
            var Q22;
            {var subQ0=sQuery(id+"F0.wireOp",EDGE,"E2.0.5.0");var subQ1=sQuery(id+"F0.wireOp",EDGE,"E0.right");var subQ2=makeQuery(id+"F0.imprint","INTERSECT",VERTEX,{"derivedFrom":[subQ1,subQ0]});Q22=makeQuery(id+"F0.imprint","IMPRINT",FACE,{"disambiguationData":[TD([[makeQuery(id+"F0.imprint","IMPRINT",EDGE,{"disambiguationData":[TD([[subQ2,-1.0]])],"derivedFrom":subQ1}),-1.0]])]});}
            var Q23;
            {var subQ0=sQuery(id+"F0.wireOp",EDGE,"E3.5.0.0");var subQ1=sQuery(id+"F0.wireOp",EDGE,"E0.top");var subQ2=makeQuery(id+"F0.imprint","INTERSECT",VERTEX,{"derivedFrom":[subQ1,subQ0]});Q23=makeQuery(id+"F0.imprint","IMPRINT",FACE,{"disambiguationData":[TD([[makeQuery(id+"F0.imprint","IMPRINT",EDGE,{"disambiguationData":[TD([[subQ2,-1.0]])],"derivedFrom":subQ1}),1.0]])]});}
            var Q24;
            {var subQ0=sQuery(id+"F0.wireOp",EDGE,"E3.4.0.0");var subQ1=sQuery(id+"F0.wireOp",EDGE,"E2.0.6.0");var subQ2=makeQuery(id+"F0.imprint","INTERSECT",VERTEX,{"derivedFrom":[subQ1,subQ0]});Q24=makeQuery(id+"F0.imprint","IMPRINT",FACE,{"disambiguationData":[TD([[makeQuery(id+"F0.imprint","IMPRINT",EDGE,{"disambiguationData":[TD([[subQ2,-1.0]])],"derivedFrom":subQ1}),-1.0]])]});}
            var Q25;
            {var subQ0=sQuery(id+"F0.wireOp",EDGE,"E3.3.0.0");var subQ1=sQuery(id+"F0.wireOp",EDGE,"E2.0.5.0");var subQ2=makeQuery(id+"F0.imprint","INTERSECT",VERTEX,{"derivedFrom":[subQ1,subQ0]});Q25=makeQuery(id+"F0.imprint","IMPRINT",FACE,{"disambiguationData":[TD([[makeQuery(id+"F0.imprint","IMPRINT",EDGE,{"disambiguationData":[TD([[subQ2,-1.0]])],"derivedFrom":subQ1}),-1.0]])]});}
            var Q26;
            {var subQ0=sQuery(id+"F0.wireOp",EDGE,"E3.2.0.0");var subQ1=sQuery(id+"F0.wireOp",EDGE,"E2.0.6.0");var subQ2=makeQuery(id+"F0.imprint","INTERSECT",VERTEX,{"derivedFrom":[subQ1,subQ0]});Q26=makeQuery(id+"F0.imprint","IMPRINT",FACE,{"disambiguationData":[TD([[makeQuery(id+"F0.imprint","IMPRINT",EDGE,{"disambiguationData":[TD([[subQ2,-1.0]])],"derivedFrom":subQ1}),-1.0]])]});}
            var Q27;
            {var subQ0=sQuery(id+"F0.wireOp",EDGE,"E3.1.0.0");var subQ1=sQuery(id+"F0.wireOp",EDGE,"E2.0.5.0");var subQ2=makeQuery(id+"F0.imprint","INTERSECT",VERTEX,{"derivedFrom":[subQ1,subQ0]});Q27=makeQuery(id+"F0.imprint","IMPRINT",FACE,{"disambiguationData":[TD([[makeQuery(id+"F0.imprint","IMPRINT",EDGE,{"disambiguationData":[TD([[subQ2,-1.0]])],"derivedFrom":subQ1}),-1.0]])]});}
            var Q28;
            {var subQ0=sQuery(id+"F0.wireOp",EDGE,"E2.0.4.0");var subQ1=sQuery(id+"F0.wireOp",EDGE,"E0.left");var subQ2=makeQuery(id+"F0.imprint","INTERSECT",VERTEX,{"derivedFrom":[subQ1,subQ0]});Q28=makeQuery(id+"F0.imprint","IMPRINT",FACE,{"disambiguationData":[TD([[makeQuery(id+"F0.imprint","IMPRINT",EDGE,{"disambiguationData":[TD([[subQ2,-1.0]])],"derivedFrom":subQ1}),1.0]])]});}
            var Q29;
            {var subQ0=sQuery(id+"F0.wireOp",EDGE,"E3.3.0.0");var subQ1=sQuery(id+"F0.wireOp",EDGE,"E0.top");var subQ2=makeQuery(id+"F0.imprint","INTERSECT",VERTEX,{"derivedFrom":[subQ1,subQ0]});Q29=makeQuery(id+"F0.imprint","IMPRINT",FACE,{"disambiguationData":[TD([[makeQuery(id+"F0.imprint","IMPRINT",EDGE,{"disambiguationData":[TD([[subQ2,-1.0]])],"derivedFrom":subQ1}),1.0]])]});}
            var Q30;
            {var subQ0=sQuery(id+"F0.wireOp",EDGE,"E3.1.0.0");var subQ1=sQuery(id+"F0.wireOp",EDGE,"E0.top");var subQ2=makeQuery(id+"F0.imprint","INTERSECT",VERTEX,{"derivedFrom":[subQ1,subQ0]});Q30=makeQuery(id+"F0.imprint","IMPRINT",FACE,{"disambiguationData":[TD([[makeQuery(id+"F0.imprint","IMPRINT",EDGE,{"disambiguationData":[TD([[subQ2,-1.0]])],"derivedFrom":subQ1}),1.0]])]});}
            var Q31;
            {var subQ0=sQuery(id+"F0.wireOp",EDGE,"E2.0.6.0");var subQ1=sQuery(id+"F0.wireOp",EDGE,"E0.left");var subQ2=makeQuery(id+"F0.imprint","INTERSECT",VERTEX,{"derivedFrom":[subQ1,subQ0]});Q31=makeQuery(id+"F0.imprint","IMPRINT",FACE,{"disambiguationData":[TD([[makeQuery(id+"F0.imprint","IMPRINT",EDGE,{"disambiguationData":[TD([[subQ2,-1.0]])],"derivedFrom":subQ1}),1.0]])]});}
            extrude(context, id + "F3", {"entities" : qUnion([Q0, Q1, Q2, Q3, Q4, Q5, Q6, Q7, Q8, Q9, Q10, Q11, Q12, Q13, Q14, Q15, Q16, Q17, Q18, Q19, Q20, Q21, Q22, Q23, Q24, Q25, Q26, Q27, Q28, Q29, Q30, Q31]), "depth" : 6 * mm, "offsetDistance" : 25 * mm, "hasSecondDirection" : true, "secondDirectionOppositeDirection" : false, "secondDirectionDepth" : 3 * mm});
        }
        {
            var Q0;
            {var subQ0=sQuery(id+"F0.wireOp",EDGE,"E3.1.0.0");var subQ1=sQuery(id+"F0.wireOp",EDGE,"E0.bottom");var subQ2=makeQuery(id+"F0.imprint","INTERSECT",VERTEX,{"derivedFrom":[subQ1,subQ0]});Q0=makeQuery(id+"F0.imprint","IMPRINT",FACE,{"disambiguationData":[TD([[makeQuery(id+"F0.imprint","IMPRINT",EDGE,{"disambiguationData":[TD([[subQ2,-1.0]])],"derivedFrom":subQ1}),-1.0]])]});}
            var Q1;
            {var subQ0=sQuery(id+"F0.wireOp",EDGE,"E2.0.1.0");var subQ1=sQuery(id+"F0.wireOp",EDGE,"E0.left");var subQ2=makeQuery(id+"F0.imprint","INTERSECT",VERTEX,{"derivedFrom":[subQ1,subQ0]});Q1=makeQuery(id+"F0.imprint","IMPRINT",FACE,{"disambiguationData":[TD([[makeQuery(id+"F0.imprint","IMPRINT",EDGE,{"disambiguationData":[TD([[subQ2,-1.0]])],"derivedFrom":subQ1}),1.0]])]});}
            var Q2;
            {var subQ0=sQuery(id+"F0.wireOp",EDGE,"E3.1.0.0");var subQ1=sQuery(id+"F0.wireOp",EDGE,"E2.0.2.0");var subQ2=makeQuery(id+"F0.imprint","INTERSECT",VERTEX,{"derivedFrom":[subQ1,subQ0]});Q2=makeQuery(id+"F0.imprint","IMPRINT",FACE,{"disambiguationData":[TD([[makeQuery(id+"F0.imprint","IMPRINT",EDGE,{"disambiguationData":[TD([[subQ2,-1.0]])],"derivedFrom":subQ1}),-1.0]])]});}
            var Q3;
            {var subQ0=sQuery(id+"F0.wireOp",EDGE,"E3.2.0.0");var subQ1=sQuery(id+"F0.wireOp",EDGE,"E2.0.1.0");var subQ2=makeQuery(id+"F0.imprint","INTERSECT",VERTEX,{"derivedFrom":[subQ1,subQ0]});Q3=makeQuery(id+"F0.imprint","IMPRINT",FACE,{"disambiguationData":[TD([[makeQuery(id+"F0.imprint","IMPRINT",EDGE,{"disambiguationData":[TD([[subQ2,-1.0]])],"derivedFrom":subQ1}),-1.0]])]});}
            var Q4;
            {var subQ0=sQuery(id+"F0.wireOp",EDGE,"E3.3.0.0");var subQ1=sQuery(id+"F0.wireOp",EDGE,"E0.bottom");var subQ2=makeQuery(id+"F0.imprint","INTERSECT",VERTEX,{"derivedFrom":[subQ1,subQ0]});Q4=makeQuery(id+"F0.imprint","IMPRINT",FACE,{"disambiguationData":[TD([[makeQuery(id+"F0.imprint","IMPRINT",EDGE,{"disambiguationData":[TD([[subQ2,-1.0]])],"derivedFrom":subQ1}),-1.0]])]});}
            var Q5;
            {var subQ0=sQuery(id+"F0.wireOp",EDGE,"E3.4.0.0");var subQ1=sQuery(id+"F0.wireOp",EDGE,"E2.0.1.0");var subQ2=makeQuery(id+"F0.imprint","INTERSECT",VERTEX,{"derivedFrom":[subQ1,subQ0]});Q5=makeQuery(id+"F0.imprint","IMPRINT",FACE,{"disambiguationData":[TD([[makeQuery(id+"F0.imprint","IMPRINT",EDGE,{"disambiguationData":[TD([[subQ2,-1.0]])],"derivedFrom":subQ1}),-1.0]])]});}
            var Q6;
            {var subQ0=sQuery(id+"F0.wireOp",EDGE,"E3.5.0.0");var subQ1=sQuery(id+"F0.wireOp",EDGE,"E2.0.2.0");var subQ2=makeQuery(id+"F0.imprint","INTERSECT",VERTEX,{"derivedFrom":[subQ1,subQ0]});Q6=makeQuery(id+"F0.imprint","IMPRINT",FACE,{"disambiguationData":[TD([[makeQuery(id+"F0.imprint","IMPRINT",EDGE,{"disambiguationData":[TD([[subQ2,-1.0]])],"derivedFrom":subQ1}),-1.0]])]});}
            var Q7;
            {var subQ0=sQuery(id+"F0.wireOp",EDGE,"E3.6.0.0");var subQ1=sQuery(id+"F0.wireOp",EDGE,"E2.0.3.0");var subQ2=makeQuery(id+"F0.imprint","INTERSECT",VERTEX,{"derivedFrom":[subQ1,subQ0]});Q7=makeQuery(id+"F0.imprint","IMPRINT",FACE,{"disambiguationData":[TD([[makeQuery(id+"F0.imprint","IMPRINT",EDGE,{"disambiguationData":[TD([[subQ2,-1.0]])],"derivedFrom":subQ1}),-1.0]])]});}
            var Q8;
            {var subQ0=sQuery(id+"F0.wireOp",EDGE,"E2.0.4.0");var subQ1=sQuery(id+"F0.wireOp",EDGE,"E0.right");var subQ2=makeQuery(id+"F0.imprint","INTERSECT",VERTEX,{"derivedFrom":[subQ1,subQ0]});Q8=makeQuery(id+"F0.imprint","IMPRINT",FACE,{"disambiguationData":[TD([[makeQuery(id+"F0.imprint","IMPRINT",EDGE,{"disambiguationData":[TD([[subQ2,-1.0]])],"derivedFrom":subQ1}),-1.0]])]});}
            var Q9;
            {var subQ0=sQuery(id+"F0.wireOp",EDGE,"E3.6.0.0");var subQ1=sQuery(id+"F0.wireOp",EDGE,"E2.0.5.0");var subQ2=makeQuery(id+"F0.imprint","INTERSECT",VERTEX,{"derivedFrom":[subQ1,subQ0]});Q9=makeQuery(id+"F0.imprint","IMPRINT",FACE,{"disambiguationData":[TD([[makeQuery(id+"F0.imprint","IMPRINT",EDGE,{"disambiguationData":[TD([[subQ2,-1.0]])],"derivedFrom":subQ1}),-1.0]])]});}
            var Q10;
            {var subQ0=sQuery(id+"F0.wireOp",EDGE,"E2.0.6.0");var subQ1=sQuery(id+"F0.wireOp",EDGE,"E0.right");var subQ2=makeQuery(id+"F0.imprint","INTERSECT",VERTEX,{"derivedFrom":[subQ1,subQ0]});Q10=makeQuery(id+"F0.imprint","IMPRINT",FACE,{"disambiguationData":[TD([[makeQuery(id+"F0.imprint","IMPRINT",EDGE,{"disambiguationData":[TD([[subQ2,-1.0]])],"derivedFrom":subQ1}),-1.0]])]});}
            var Q11;
            {var subQ0=sQuery(id+"F0.wireOp",EDGE,"E3.5.0.0");var subQ1=sQuery(id+"F0.wireOp",EDGE,"E2.0.4.0");var subQ2=makeQuery(id+"F0.imprint","INTERSECT",VERTEX,{"derivedFrom":[subQ1,subQ0]});Q11=makeQuery(id+"F0.imprint","IMPRINT",FACE,{"disambiguationData":[TD([[makeQuery(id+"F0.imprint","IMPRINT",EDGE,{"disambiguationData":[TD([[subQ2,-1.0]])],"derivedFrom":subQ1}),-1.0]])]});}
            var Q12;
            {var subQ0=sQuery(id+"F0.wireOp",EDGE,"E3.4.0.0");var subQ1=sQuery(id+"F0.wireOp",EDGE,"E2.0.3.0");var subQ2=makeQuery(id+"F0.imprint","INTERSECT",VERTEX,{"derivedFrom":[subQ1,subQ0]});Q12=makeQuery(id+"F0.imprint","IMPRINT",FACE,{"disambiguationData":[TD([[makeQuery(id+"F0.imprint","IMPRINT",EDGE,{"disambiguationData":[TD([[subQ2,-1.0]])],"derivedFrom":subQ1}),-1.0]])]});}
            var Q13;
            {var subQ0=sQuery(id+"F0.wireOp",EDGE,"E3.3.0.0");var subQ1=sQuery(id+"F0.wireOp",EDGE,"E2.0.2.0");var subQ2=makeQuery(id+"F0.imprint","INTERSECT",VERTEX,{"derivedFrom":[subQ1,subQ0]});Q13=makeQuery(id+"F0.imprint","IMPRINT",FACE,{"disambiguationData":[TD([[makeQuery(id+"F0.imprint","IMPRINT",EDGE,{"disambiguationData":[TD([[subQ2,-1.0]])],"derivedFrom":subQ1}),-1.0]])]});}
            var Q14;
            {var subQ0=sQuery(id+"F0.wireOp",EDGE,"E3.5.0.0");var subQ1=sQuery(id+"F0.wireOp",EDGE,"E0.bottom");var subQ2=makeQuery(id+"F0.imprint","INTERSECT",VERTEX,{"derivedFrom":[subQ1,subQ0]});Q14=makeQuery(id+"F0.imprint","IMPRINT",FACE,{"disambiguationData":[TD([[makeQuery(id+"F0.imprint","IMPRINT",EDGE,{"disambiguationData":[TD([[subQ2,-1.0]])],"derivedFrom":subQ1}),-1.0]])]});}
            var Q15;
            {var subQ0=sQuery(id+"F0.wireOp",EDGE,"E3.6.0.0");var subQ1=sQuery(id+"F0.wireOp",EDGE,"E2.0.1.0");var subQ2=makeQuery(id+"F0.imprint","INTERSECT",VERTEX,{"derivedFrom":[subQ1,subQ0]});Q15=makeQuery(id+"F0.imprint","IMPRINT",FACE,{"disambiguationData":[TD([[makeQuery(id+"F0.imprint","IMPRINT",EDGE,{"disambiguationData":[TD([[subQ2,-1.0]])],"derivedFrom":subQ1}),-1.0]])]});}
            var Q16;
            {var subQ0=sQuery(id+"F0.wireOp",EDGE,"E2.0.2.0");var subQ1=sQuery(id+"F0.wireOp",EDGE,"E0.right");var subQ2=makeQuery(id+"F0.imprint","INTERSECT",VERTEX,{"derivedFrom":[subQ1,subQ0]});Q16=makeQuery(id+"F0.imprint","IMPRINT",FACE,{"disambiguationData":[TD([[makeQuery(id+"F0.imprint","IMPRINT",EDGE,{"disambiguationData":[TD([[subQ2,-1.0]])],"derivedFrom":subQ1}),-1.0]])]});}
            var Q17;
            {var subQ0=sQuery(id+"F0.wireOp",EDGE,"E0.right");var subQ1=sQuery(id+"F0.wireOp",EDGE,"E0.bottom");var subQ2=makeQuery(id+"F0.imprint","INTERSECT",VERTEX,{"derivedFrom":[subQ1,subQ0]});Q17=makeQuery(id+"F0.imprint","IMPRINT",FACE,{"disambiguationData":[TD([[makeQuery(id+"F0.imprint","IMPRINT",EDGE,{"disambiguationData":[TD([[subQ2,1.0]])],"derivedFrom":subQ1}),-1.0]])]});}
            var Q18;
            {var subQ0=sQuery(id+"F0.wireOp",EDGE,"E3.3.0.0");var subQ1=sQuery(id+"F0.wireOp",EDGE,"E2.0.4.0");var subQ2=makeQuery(id+"F0.imprint","INTERSECT",VERTEX,{"derivedFrom":[subQ1,subQ0]});Q18=makeQuery(id+"F0.imprint","IMPRINT",FACE,{"disambiguationData":[TD([[makeQuery(id+"F0.imprint","IMPRINT",EDGE,{"disambiguationData":[TD([[subQ2,-1.0]])],"derivedFrom":subQ1}),-1.0]])]});}
            var Q19;
            {var subQ0=sQuery(id+"F0.wireOp",EDGE,"E3.2.0.0");var subQ1=sQuery(id+"F0.wireOp",EDGE,"E2.0.3.0");var subQ2=makeQuery(id+"F0.imprint","INTERSECT",VERTEX,{"derivedFrom":[subQ1,subQ0]});Q19=makeQuery(id+"F0.imprint","IMPRINT",FACE,{"disambiguationData":[TD([[makeQuery(id+"F0.imprint","IMPRINT",EDGE,{"disambiguationData":[TD([[subQ2,-1.0]])],"derivedFrom":subQ1}),-1.0]])]});}
            var Q20;
            {var subQ0=sQuery(id+"F0.wireOp",EDGE,"E2.0.3.0");var subQ1=sQuery(id+"F0.wireOp",EDGE,"E0.left");var subQ2=makeQuery(id+"F0.imprint","INTERSECT",VERTEX,{"derivedFrom":[subQ1,subQ0]});Q20=makeQuery(id+"F0.imprint","IMPRINT",FACE,{"disambiguationData":[TD([[makeQuery(id+"F0.imprint","IMPRINT",EDGE,{"disambiguationData":[TD([[subQ2,-1.0]])],"derivedFrom":subQ1}),1.0]])]});}
            var Q21;
            {var subQ0=sQuery(id+"F0.wireOp",EDGE,"E3.1.0.0");var subQ1=sQuery(id+"F0.wireOp",EDGE,"E2.0.4.0");var subQ2=makeQuery(id+"F0.imprint","INTERSECT",VERTEX,{"derivedFrom":[subQ1,subQ0]});Q21=makeQuery(id+"F0.imprint","IMPRINT",FACE,{"disambiguationData":[TD([[makeQuery(id+"F0.imprint","IMPRINT",EDGE,{"disambiguationData":[TD([[subQ2,-1.0]])],"derivedFrom":subQ1}),-1.0]])]});}
            var Q22;
            {var subQ0=sQuery(id+"F0.wireOp",EDGE,"E3.2.0.0");var subQ1=sQuery(id+"F0.wireOp",EDGE,"E2.0.5.0");var subQ2=makeQuery(id+"F0.imprint","INTERSECT",VERTEX,{"derivedFrom":[subQ1,subQ0]});Q22=makeQuery(id+"F0.imprint","IMPRINT",FACE,{"disambiguationData":[TD([[makeQuery(id+"F0.imprint","IMPRINT",EDGE,{"disambiguationData":[TD([[subQ2,-1.0]])],"derivedFrom":subQ1}),-1.0]])]});}
            var Q23;
            {var subQ0=sQuery(id+"F0.wireOp",EDGE,"E3.3.0.0");var subQ1=sQuery(id+"F0.wireOp",EDGE,"E2.0.6.0");var subQ2=makeQuery(id+"F0.imprint","INTERSECT",VERTEX,{"derivedFrom":[subQ1,subQ0]});Q23=makeQuery(id+"F0.imprint","IMPRINT",FACE,{"disambiguationData":[TD([[makeQuery(id+"F0.imprint","IMPRINT",EDGE,{"disambiguationData":[TD([[subQ2,-1.0]])],"derivedFrom":subQ1}),-1.0]])]});}
            var Q24;
            {var subQ0=sQuery(id+"F0.wireOp",EDGE,"E3.4.0.0");var subQ1=sQuery(id+"F0.wireOp",EDGE,"E0.top");var subQ2=makeQuery(id+"F0.imprint","INTERSECT",VERTEX,{"derivedFrom":[subQ1,subQ0]});Q24=makeQuery(id+"F0.imprint","IMPRINT",FACE,{"disambiguationData":[TD([[makeQuery(id+"F0.imprint","IMPRINT",EDGE,{"disambiguationData":[TD([[subQ2,-1.0]])],"derivedFrom":subQ1}),1.0]])]});}
            var Q25;
            {var subQ0=sQuery(id+"F0.wireOp",EDGE,"E3.5.0.0");var subQ1=sQuery(id+"F0.wireOp",EDGE,"E2.0.6.0");var subQ2=makeQuery(id+"F0.imprint","INTERSECT",VERTEX,{"derivedFrom":[subQ1,subQ0]});Q25=makeQuery(id+"F0.imprint","IMPRINT",FACE,{"disambiguationData":[TD([[makeQuery(id+"F0.imprint","IMPRINT",EDGE,{"disambiguationData":[TD([[subQ2,-1.0]])],"derivedFrom":subQ1}),-1.0]])]});}
            var Q26;
            {var subQ0=sQuery(id+"F0.wireOp",EDGE,"E3.4.0.0");var subQ1=sQuery(id+"F0.wireOp",EDGE,"E2.0.5.0");var subQ2=makeQuery(id+"F0.imprint","INTERSECT",VERTEX,{"derivedFrom":[subQ1,subQ0]});Q26=makeQuery(id+"F0.imprint","IMPRINT",FACE,{"disambiguationData":[TD([[makeQuery(id+"F0.imprint","IMPRINT",EDGE,{"disambiguationData":[TD([[subQ2,-1.0]])],"derivedFrom":subQ1}),-1.0]])]});}
            var Q27;
            {var subQ0=sQuery(id+"F0.wireOp",EDGE,"E3.6.0.0");var subQ1=sQuery(id+"F0.wireOp",EDGE,"E0.top");var subQ2=makeQuery(id+"F0.imprint","INTERSECT",VERTEX,{"derivedFrom":[subQ1,subQ0]});Q27=makeQuery(id+"F0.imprint","IMPRINT",FACE,{"disambiguationData":[TD([[makeQuery(id+"F0.imprint","IMPRINT",EDGE,{"disambiguationData":[TD([[subQ2,-1.0]])],"derivedFrom":subQ1}),1.0]])]});}
            var Q28;
            {var subQ0=sQuery(id+"F0.wireOp",EDGE,"E3.2.0.0");var subQ1=sQuery(id+"F0.wireOp",EDGE,"E0.top");var subQ2=makeQuery(id+"F0.imprint","INTERSECT",VERTEX,{"derivedFrom":[subQ1,subQ0]});Q28=makeQuery(id+"F0.imprint","IMPRINT",FACE,{"disambiguationData":[TD([[makeQuery(id+"F0.imprint","IMPRINT",EDGE,{"disambiguationData":[TD([[subQ2,-1.0]])],"derivedFrom":subQ1}),1.0]])]});}
            var Q29;
            {var subQ0=sQuery(id+"F0.wireOp",EDGE,"E3.1.0.0");var subQ1=sQuery(id+"F0.wireOp",EDGE,"E2.0.6.0");var subQ2=makeQuery(id+"F0.imprint","INTERSECT",VERTEX,{"derivedFrom":[subQ1,subQ0]});Q29=makeQuery(id+"F0.imprint","IMPRINT",FACE,{"disambiguationData":[TD([[makeQuery(id+"F0.imprint","IMPRINT",EDGE,{"disambiguationData":[TD([[subQ2,-1.0]])],"derivedFrom":subQ1}),-1.0]])]});}
            var Q30;
            {var subQ0=sQuery(id+"F0.wireOp",EDGE,"E2.0.5.0");var subQ1=sQuery(id+"F0.wireOp",EDGE,"E0.left");var subQ2=makeQuery(id+"F0.imprint","INTERSECT",VERTEX,{"derivedFrom":[subQ1,subQ0]});Q30=makeQuery(id+"F0.imprint","IMPRINT",FACE,{"disambiguationData":[TD([[makeQuery(id+"F0.imprint","IMPRINT",EDGE,{"disambiguationData":[TD([[subQ2,-1.0]])],"derivedFrom":subQ1}),1.0]])]});}
            var Q31;
            {var subQ0=sQuery(id+"F0.wireOp",EDGE,"E0.left");var subQ1=sQuery(id+"F0.wireOp",EDGE,"E0.top");var subQ2=makeQuery(id+"F0.imprint","INTERSECT",VERTEX,{"derivedFrom":[subQ1,subQ0]});Q31=makeQuery(id+"F0.imprint","IMPRINT",FACE,{"disambiguationData":[TD([[makeQuery(id+"F0.imprint","IMPRINT",EDGE,{"disambiguationData":[TD([[subQ2,-1.0]])],"derivedFrom":subQ1}),1.0]])]});}
            extrude(context, id + "F4", {"entities" : qUnion([Q0, Q1, Q2, Q3, Q4, Q5, Q6, Q7, Q8, Q9, Q10, Q11, Q12, Q13, Q14, Q15, Q16, Q17, Q18, Q19, Q20, Q21, Q22, Q23, Q24, Q25, Q26, Q27, Q28, Q29, Q30, Q31]), "depth" : 6 * mm, "offsetDistance" : 25 * mm, "hasSecondDirection" : true, "secondDirectionOppositeDirection" : false, "secondDirectionDepth" : 3 * mm});
        }
    });
